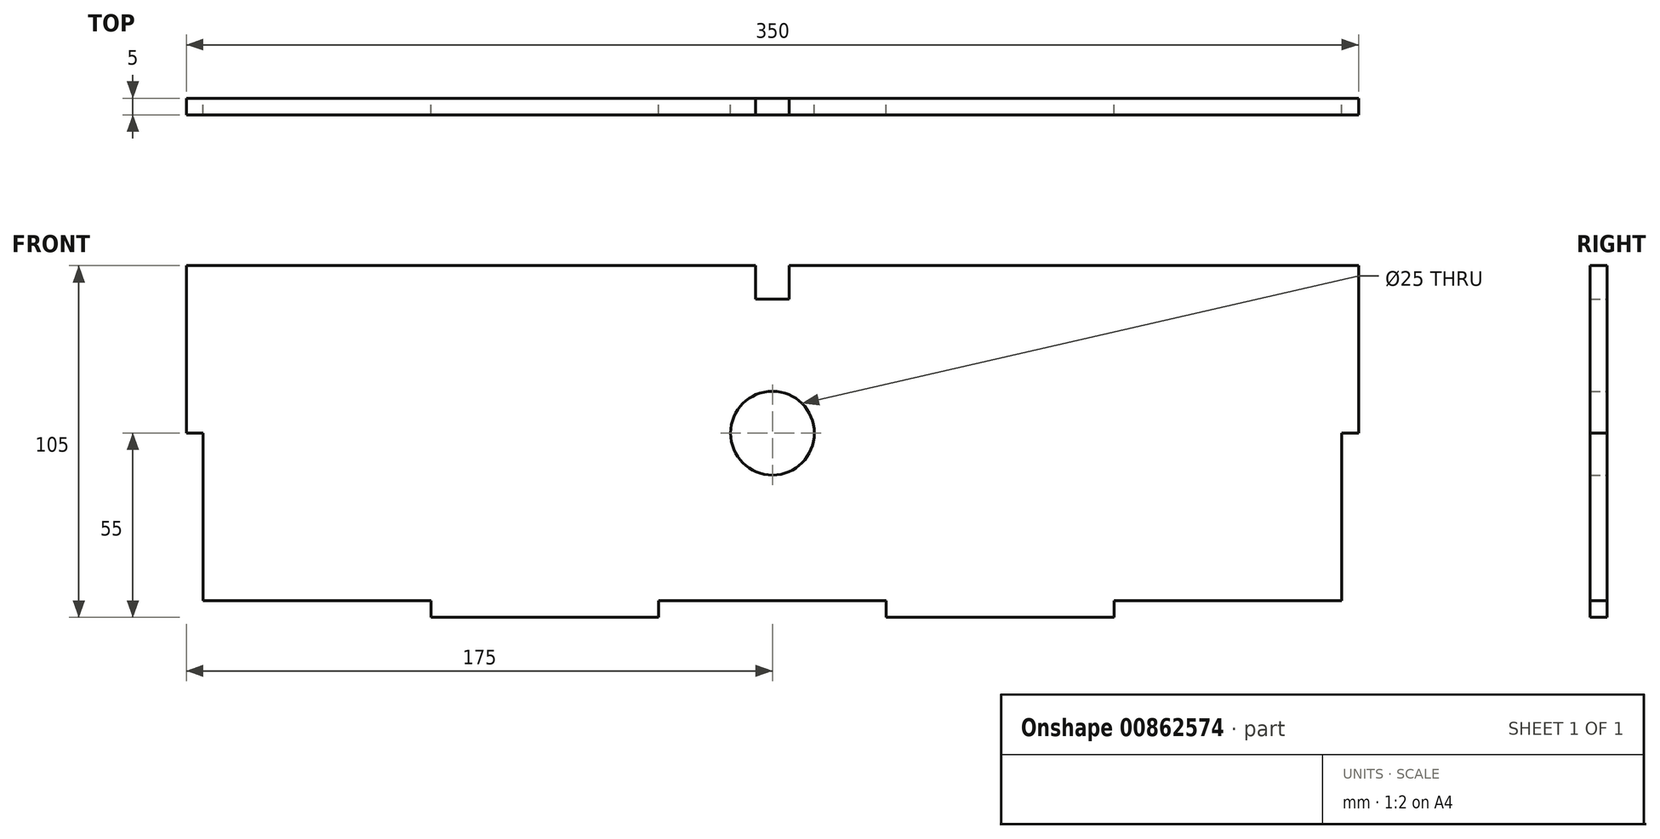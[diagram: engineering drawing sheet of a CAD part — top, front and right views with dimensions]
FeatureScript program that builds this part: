
annotation { "Feature Type Name" : "Feature", "Feature Type Description" : "" }
export const myFeature = defineFeature(function(context is Context, id is Id, definition is map)
    precondition{}
    {
        {
            var Q0;
            Q0=qCreatedBy(makeId("Front.planeOp"),FACE);
            var sketch = newSketch(context, id + "F0", { "sketchPlane" : qUnion([Q0])});
            skLineSegment(sketch, "E0.bottom", {"start": v(170, -50) * mm, "end": v(-170, -50) * mm});
            skLineSegment(sketch, "E0.top", {"start": v(170, 50) * mm, "end": v(5, 50) * mm});
            skLineSegment(sketch, "E0.left", {"start": v(170, -50) * mm, "end": v(170, 50) * mm});
            skLineSegment(sketch, "E0.right", {"start": v(-170, -50) * mm, "end": v(-170, 50) * mm});
            skPoint(sketch, "E0.middle", {"position": v(0, 0) * mm});
            skLineSegment(sketch, "E1", {"start": v(-102, -50) * mm, "end": v(-102, -55) * mm});
            skLineSegment(sketch, "E2", {"start": v(-102, -55) * mm, "end": v(-34, -55) * mm});
            skLineSegment(sketch, "E3", {"start": v(-34, -55) * mm, "end": v(-34, -50) * mm});
            skLineSegment(sketch, "E4", {"start": v(0, 80.34) * mm, "end": v(0, -109.87) * mm});
            skPoint(sketch, "E4.endSnap0", {"position": v(0, -50) * mm});
            skLineSegment(sketch, "E5.MirrorCS", {"start": v(102, -50) * mm, "end": v(102, -55) * mm});
            skLineSegment(sketch, "E6.MirrorCS", {"start": v(102, -55) * mm, "end": v(34, -55) * mm});
            skLineSegment(sketch, "E7.MirrorCS", {"start": v(34, -55) * mm, "end": v(34, -50) * mm});
            skCircle(sketch, "E8", {"center": v(0, 0) * mm, "radius": 12.5 * mm});
            skLineSegment(sketch, "E9", {"start": v(-170, 50) * mm, "end": v(-175, 50) * mm});
            skLineSegment(sketch, "E10", {"start": v(-175, 50) * mm, "end": v(-175, 0) * mm});
            skLineSegment(sketch, "E11", {"start": v(-175, 0) * mm, "end": v(-170, 0) * mm});
            skLineSegment(sketch, "E12.MirrorCS", {"start": v(170, 50) * mm, "end": v(175, 50) * mm});
            skLineSegment(sketch, "E13.MirrorCS", {"start": v(175, 50) * mm, "end": v(175, 0) * mm});
            skLineSegment(sketch, "E14.MirrorCS", {"start": v(175, 0) * mm, "end": v(170, 0) * mm});
            skLineSegment(sketch, "E15", {"start": v(-5, 50) * mm, "end": v(-5, 40) * mm});
            skLineSegment(sketch, "E16", {"start": v(-5, 40) * mm, "end": v(5, 40) * mm});
            skLineSegment(sketch, "E17", {"start": v(5, 40) * mm, "end": v(5, 50) * mm});
            skLineSegment(sketch, "E18.trimOffspring", {"start": v(-5, 50) * mm, "end": v(-170, 50) * mm});
            skSolve(sketch);
        }
        {
            var Q0;
            Q0=qSketchRegion(id+"F0",true);
            extrude(context, id + "F1", {"entities" : qUnion([Q0]), "depth" : 5 * mm, "offsetDistance" : 25 * mm});
        }
    });
